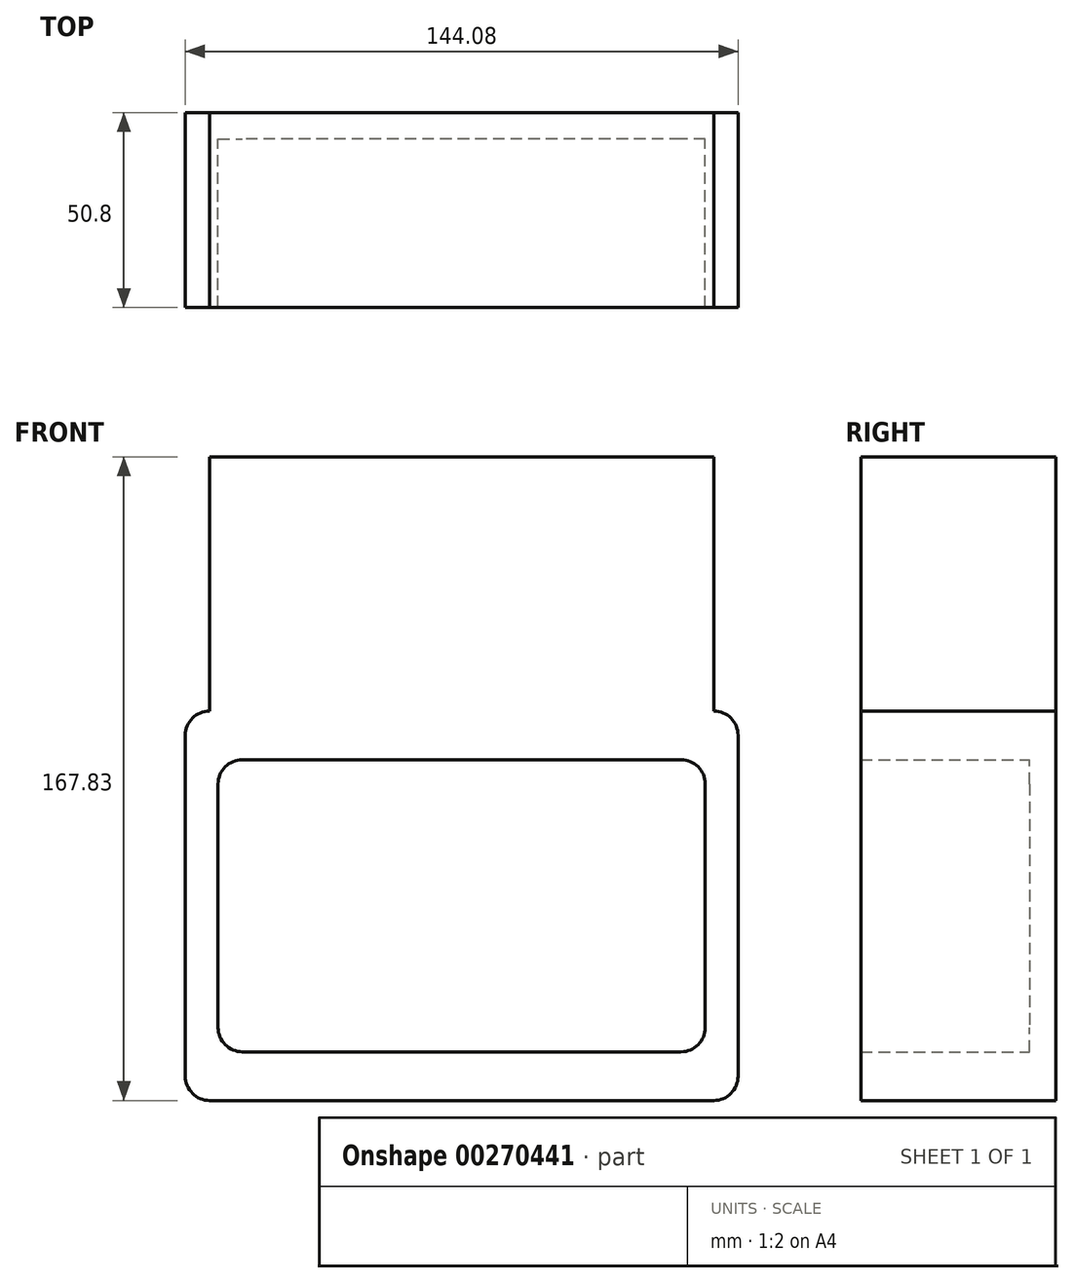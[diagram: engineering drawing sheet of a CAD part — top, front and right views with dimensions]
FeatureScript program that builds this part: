
annotation { "Feature Type Name" : "Feature", "Feature Type Description" : "" }
export const myFeature = defineFeature(function(context is Context, id is Id, definition is map)
    precondition{}
    {
        {
            var Q0;
            Q0=qCreatedBy(makeId("Front.planeOp"),FACE);
            var sketch = newSketch(context, id + "F0", { "sketchPlane" : qUnion([Q0])});
            skLineSegment(sketch, "E0.bottom", {"start": v(57.15, 38.1) * mm, "end": v(-57.15, 38.1) * mm});
            skLineSegment(sketch, "E0.top", {"start": v(57.15, -38.1) * mm, "end": v(-57.15, -38.1) * mm});
            skLineSegment(sketch, "E0.left", {"start": v(63.5, 31.75) * mm, "end": v(63.5, -31.75) * mm});
            skLineSegment(sketch, "E0.right", {"start": v(-63.5, 31.75) * mm, "end": v(-63.5, -31.75) * mm});
            skPoint(sketch, "E0.middle", {"position": v(0, 0) * mm});
            skPoint(sketch, "E1.visualSharp", {"position": v(-63.5, 38.1) * mm});
            skArc(sketch, "E1.filletArc", {"start": v(-57.15, 38.1) * mm, "mid": v(-61.64, 36.24) * mm, "end": v(-63.5, 31.75) * mm});
            skPoint(sketch, "E2.visualSharp", {"position": v(63.5, 38.1) * mm});
            skArc(sketch, "E2.filletArc", {"start": v(63.5, 31.75) * mm, "mid": v(61.64, 36.24) * mm, "end": v(57.15, 38.1) * mm});
            skPoint(sketch, "E3.visualSharp", {"position": v(63.5, -38.1) * mm});
            skArc(sketch, "E3.filletArc", {"start": v(57.15, -38.1) * mm, "mid": v(61.64, -36.24) * mm, "end": v(63.5, -31.75) * mm});
            skPoint(sketch, "E4.visualSharp", {"position": v(-63.5, -38.1) * mm});
            skArc(sketch, "E4.filletArc", {"start": v(-63.5, -31.75) * mm, "mid": v(-61.64, -36.24) * mm, "end": v(-57.15, -38.1) * mm});
            skLineSegment(sketch, "E5.bottom", {"start": v(-65.7, 50.8) * mm, "end": v(65.7, 50.8) * mm});
            skLineSegment(sketch, "E5.top", {"start": v(-65.7, -50.8) * mm, "end": v(65.7, -50.8) * mm});
            skLineSegment(sketch, "E5.left", {"start": v(-72.04, 44.45) * mm, "end": v(-72.04, -44.45) * mm});
            skLineSegment(sketch, "E5.right", {"start": v(72.04, 44.45) * mm, "end": v(72.04, -44.45) * mm});
            skPoint(sketch, "E6.visualSharp", {"position": v(-72.04, 50.8) * mm});
            skArc(sketch, "E6.filletArc", {"start": v(-65.7, 50.8) * mm, "mid": v(-70.18, 48.94) * mm, "end": v(-72.04, 44.45) * mm});
            skPoint(sketch, "E7.visualSharp", {"position": v(72.04, 50.8) * mm});
            skArc(sketch, "E7.filletArc", {"start": v(72.04, 44.45) * mm, "mid": v(70.18, 48.94) * mm, "end": v(65.7, 50.8) * mm});
            skPoint(sketch, "E8.visualSharp", {"position": v(72.04, -50.8) * mm});
            skArc(sketch, "E8.filletArc", {"start": v(65.7, -50.8) * mm, "mid": v(70.18, -48.94) * mm, "end": v(72.04, -44.45) * mm});
            skPoint(sketch, "E9.visualSharp", {"position": v(-72.04, -50.8) * mm});
            skArc(sketch, "E9.filletArc", {"start": v(-72.04, -44.45) * mm, "mid": v(-70.18, -48.94) * mm, "end": v(-65.7, -50.8) * mm});
            skLineSegment(sketch, "E10.left", {"start": v(-65.7, 50.8) * mm, "end": v(-65.7, 50.8) * mm});
            skLineSegment(sketch, "E10.right", {"start": v(65.7, 50.8) * mm, "end": v(65.7, 50.8) * mm});
            skLineSegment(sketch, "E11.bottom", {"start": v(65.7, 50.8) * mm, "end": v(-65.7, 50.8) * mm});
            skLineSegment(sketch, "E11.top", {"start": v(65.7, 117.03) * mm, "end": v(-65.7, 117.03) * mm});
            skLineSegment(sketch, "E11.left", {"start": v(65.7, 50.8) * mm, "end": v(65.7, 117.03) * mm});
            skLineSegment(sketch, "E11.right", {"start": v(-65.7, 50.8) * mm, "end": v(-65.7, 117.03) * mm});
            skLineSegment(sketch, "E12", {"start": v(0, 117.03) * mm, "end": v(0, 50.8) * mm});
            skPoint(sketch, "E13", {"position": v(0, 83.92) * mm});
            skSolve(sketch);
        }
        {
            var Q0;
            Q0=makeQuery(id+"F0.imprint","IMPRINT",FACE,{"disambiguationData":[TD([[makeQuery(id+"F0.imprint","IMPRINT",EDGE,{"derivedFrom":sQuery(id+"F0.wireOp",EDGE,"E0.bottom")}),1.0]])]});
            extrude(context, id + "F1", {"entities" : qUnion([Q0]), "depth" : 6.86 * mm});
        }
        {
            var Q0;
            Q0 = qSketchRegion(id + "F0", true);
            extrude(context, id + "F2", {"entities" : qUnion([Q0]), "operationType" : NewBodyOperationType.ADD, "depth" : 50.8 * mm});
        }
    });
